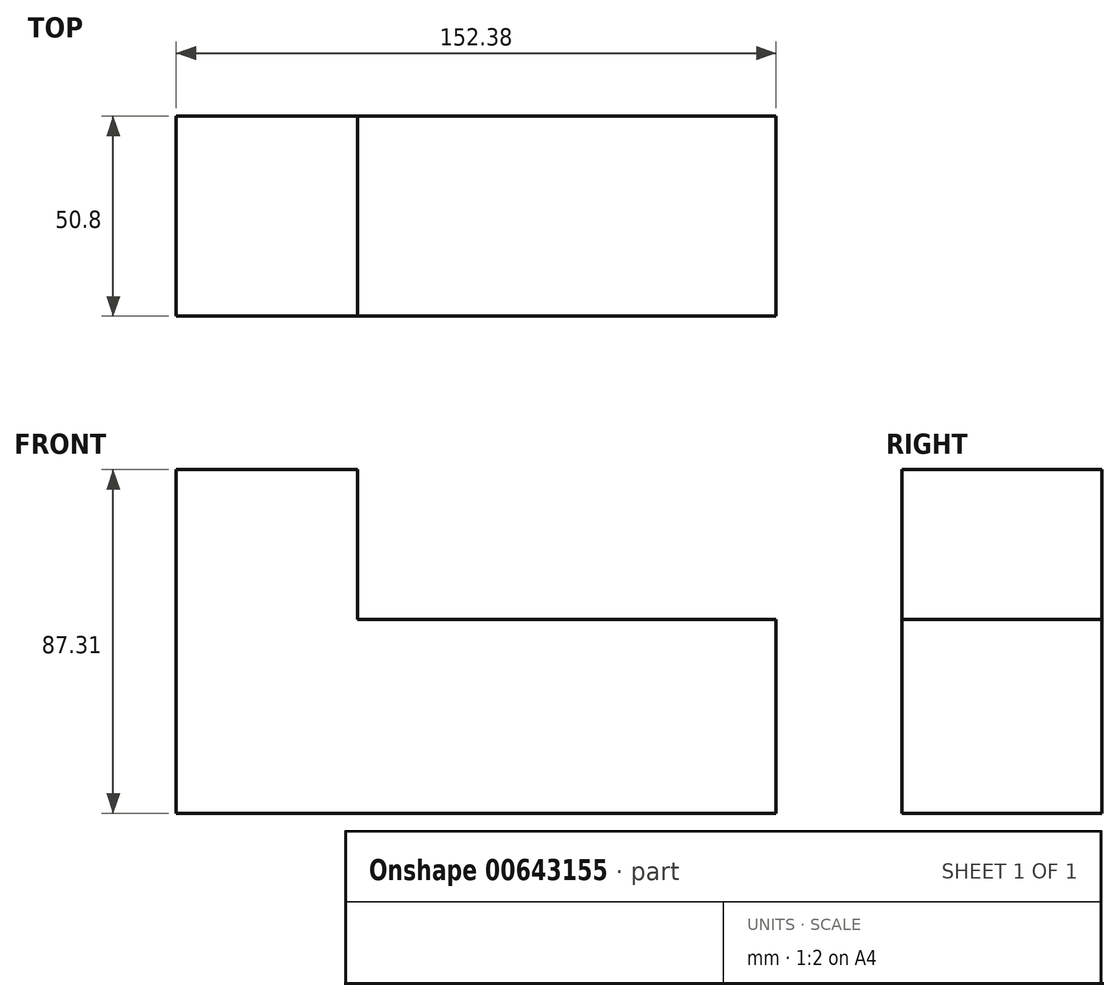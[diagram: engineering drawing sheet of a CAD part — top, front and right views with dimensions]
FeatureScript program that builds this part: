
annotation { "Feature Type Name" : "Feature", "Feature Type Description" : "" }
export const myFeature = defineFeature(function(context is Context, id is Id, definition is map)
    precondition{}
    {
        {
            var Q0;
            Q0=qCreatedBy(makeId("Front.planeOp"),FACE);
            var sketch = newSketch(context, id + "F0", { "sketchPlane" : qUnion([Q0])});
            skLineSegment(sketch, "E0", {"start": v(-44.8, 55.48) * mm, "end": v(-44.8, -31.83) * mm});
            skLineSegment(sketch, "E1", {"start": v(-44.8, -31.83) * mm, "end": v(107.58, -31.83) * mm});
            skLineSegment(sketch, "E2", {"start": v(107.58, -31.83) * mm, "end": v(107.58, 17.38) * mm});
            skLineSegment(sketch, "E3", {"start": v(1.22, 17.38) * mm, "end": v(107.58, 17.38) * mm});
            skLineSegment(sketch, "E4", {"start": v(1.22, 17.38) * mm, "end": v(1.22, 55.48) * mm});
            skLineSegment(sketch, "E5", {"start": v(1.22, 55.48) * mm, "end": v(-44.8, 55.48) * mm});
            skSolve(sketch);
        }
        {
            var Q0;
            Q0 = qSketchRegion(id + "F0", true);
            extrude(context, id + "F1", {"entities" : qUnion([Q0]), "depth" : 50.8 * mm, "offsetDistance" : 25.4 * mm});
        }
    });
